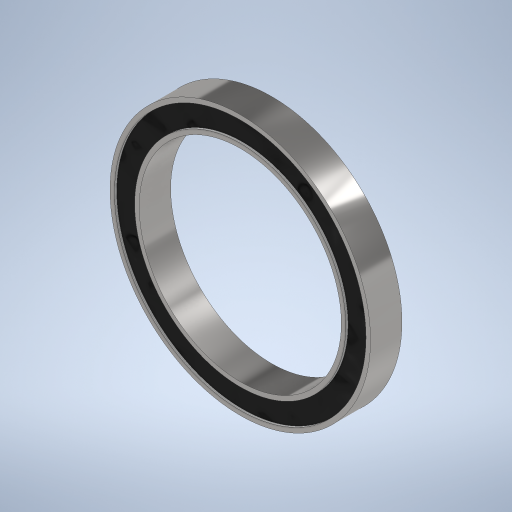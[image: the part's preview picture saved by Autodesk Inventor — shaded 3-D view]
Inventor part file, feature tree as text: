
AUTODESK INVENTOR PART (.ipt)
format: ipt  version: 2023 (Build 270158000, 158)  size: 296,448 bytes
history: native  units: mm
features: extrude x3, sketch x3, projected_geometry x1
ambient origin geometry x8: Origin, YZ Plane, XZ Plane, XY Plane, X Axis, Y Axis, Z Axis, Center Point
bodies: Solid1 (feature_tree)
feature tree (7):
  extrude  "Extrusion1"  Depth=45.0mm
  extrude  "Extrusion2"  Depth=7.0mm
  extrude  "Extrusion3"  Depth=0.5mm TaperAngle=0.0deg
  sketch  "Sketch1"  dims[d0=58.0mm d1=45.0mm]
  sketch  "Sketch2"  dims[d2=7.0mm d3=0.0mm d4=1.0mm]
  projected_geometry  "Projected Loop1"
  sketch  "Sketch3"  dims[d5=1.0mm d6=0.5mm d7=0.0mm d8=0.5mm d9=0.0mm]
